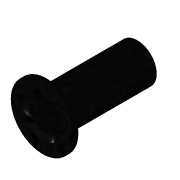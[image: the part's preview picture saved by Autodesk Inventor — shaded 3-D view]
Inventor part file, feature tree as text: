
AUTODESK INVENTOR PART (.ipt)
format: ipt  version: 2022 (Build 260153000, 153)  size: 136,192 bytes
history: native  units: mm
features: reference x4, other x4, extrude x3, sketch x3, chamfer x1, plane x1
ambient origin geometry x8: Origin, YZ Plane, XZ Plane, XY Plane, X Axis, Y Axis, Z Axis, Center Point
bodies: Volumenkörper1 (feature_tree)
feature tree (16):
  extrude  "Extrusion1"  Depth=8.1mm
  extrude  "Extrusion2"  Depth=1.0mm
  chamfer  "Fase1"  Distance=1.0mm
  sketch  "Skizze3"  dims[d7=1.0mm d8=2.0mm d9=45.0deg d10=18.0mm d11=0.0mm d12=6.0mm d13=0.0mm]
  plane  "Arbeitsebene1"
  extrude  "Extrusion3"  Depth=18.0mm TaperAngle=0.0deg
  sketch  "Skizze1"  dims[d0=0.1mm d1=8.1mm]
  reference  "Referenz1"
  reference  "Referenz2"
  sketch  "Skizze2"  dims[d2=6.0mm d3=0.0mm d4=0.5mm d5=1.0mm d6=0.0mm]
  reference  "Referenz3"
  reference  "Referenz4"
  other  "Assembly_ETL_v0.iam"
  other  "50_ETL_28by_coil:1"
  other  "50_ETL_Spring_v0:2"
  other  "50_ETL_Membrane_v0:1"
